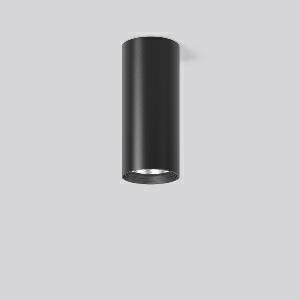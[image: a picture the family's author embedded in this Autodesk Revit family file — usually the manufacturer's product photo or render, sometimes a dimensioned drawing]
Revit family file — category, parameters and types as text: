
# Revit family: heledon_mini_a_931201_003_76_b822
name_source: partatom
category: Lighting Fixtures
units: mm (PartAtom-declared; Revit-internal decimal feet)

## family parameters
Cut with Voids When Loaded = No
Host = Face
Light Source = No
Part Type = Normal
Room Calculation Point = No
Round Connector Dimension = Use Diameter
Shared = No

## types (1)
- HELEDON mini A (1 x LED Modul 930, 2450 lm, 3000)
    Apparent Load = 20 VA
    Approval mark = CE
    CIE Flux Codes = 99 100 100 100 100
    Color Rendering = 90
    Color Temperature = 3000
    Default Elevation = 1800 mm
    Description = Series: HELEDON mini
Cylindrical surface-mounted downlight. Housing: die-cast aluminium, powder-coated. Internal ceiling frame polycarbonate with bayonet mounting. Black plastic ring and recessed LED to prevent glare from the side. Optical assembly with reflector made of MIRO-Silver with 98% total light reflection for outstanding efficiency - can be changed without tools. Best colour rendering index Ra>90. Suitable for Ceiling mounting. Easy installation with a separate ceiling frame with bayonet mounting and plug connection. Driver integrated. Connected via plug-in connector. High quality converter without flickering and stroboscopic effect. The following accessories can be mounted without use of tools: interchangeable lenses, decorative glasses, honeycomb louvre, clear and frosted diffusers, white interchangeable plastic ring. 
Colour: deep black, matt (RAL 9005)
Diameter: 87 mm
Height: 197 mm
Lamp: LED
Socket: without socket
Colour temperature: 3000K
Colour rendering index (CRI): 92
System power: 20 W
Rated luminous flux: 2450 lm
Luminous efficiency: 123 lm/W
Control gear: Converter, dimmable, DALI
Protection class: I
Type of protection: IP 20
    Height = 197 mm
    Lamp = 1 x LED Modul 930
    Lamp Light Flux = 2450 lm
    Lamp count = 1
    Length = 87 mm
    Lifetime = 50000 h
    Luminous efficacy = 123 lm/W
    Manufacturer = RZB
    ModVariant = No
    Model = 931201.003.76
    Mounting Place = Ceiling
    Mounting Type = Surface mounted
    Number of Poles = 1
    OnlyDefault = Yes
    Power Factor = 1
    Product Name = HELEDON mini A
    Product group = Surface mounted downlights
    ProductGroupID = 302
    Protection Class = Protection class I
    Protection Degree = IP 20
    RLX_Detail_Level = 1
    RLX_Emergency_Light_Flux = 0 lm
    RLX_Emergency_Type = 0
    RLX_Emergency_Type_DB = No
    RlxData = <blob elided: 106505 chars, md5=452de13c>
    Socket = socket
    Standby Power = 0 W
    System Light Flux = 2450 lm
    System Power = 20 W
    Type Comments = Product without accessories
    Type Image = 931188.003.jpg
    URL = http://relux.com
    VarID = ---
    Voltage = 230 V
    Voltage Range = 220-240 V
    Weight = 0.00 kg
    Width = 0 mm  [stored 0 ft]

note: [stored X ft] marks values corroborated as IEEE doubles in the binary element streams (Revit-internal decimal feet)

## geometry (parser evidence)
native form markers: Blend x4, Sweep x10
no freeform markers — native parametric forms only
